# Revit family: LVS1HD
name_source: partatom
category: Communication Devices
units: mm (PartAtom-declared; Revit-internal decimal feet)

## family parameters
Cut with Voids When Loaded = No
Host = Face
Maintain Annotation Orientation = No
OmniClass Number = 23.85.80.11.27
OmniClass Title = Lighting Controls
Part Type = Normal
Room Calculation Point = No
Round Connector Dimension = Use Diameter
Shared = Yes

## types (1)
- LVS1HD
    Assembly Code = D5090
    Blue = Plastic - Blue
    Default Elevation = 48 "
    Description = Our LVS1HD heavy duty wall switch is ideal for high abuse applications where standard plastic low voltage wall switch stations are not suitable. The LVS1HD looks like a standard wall switch except has a spring loaded return to center toggle action that can be connected to lighting controls expecting a dry contact momentary input.
    Feartures = • Gang-able, uses standard switch plate (not supplied)
• Abuse resistant nylon toggle
• UL 94V-2 flammability rating
• Heavy duty Silver Alloy contacts
• Compatible with CX panel low voltage inputs
• Use NXCI Contact Interface module for compatibility with NX™
distributed controls
• UL listed, CSA certified
• Low voltage device: 24 VDC
    Housing Material = Metal-Galvanized_Steel
    Manufacturer = NX Lighting Controls
    Metal = Steel, Non-Alloy
    Model = LVS1HD
    Switch = Porcelain, Ivory
    Type Comments = Heavy Duty Low Voltage Wall Switch
    URL = https://www.currentlighting.com
    Warranty = 5-Years Warranty

## geometry (parser evidence)
native form markers: Sweep x2
no freeform markers — native parametric forms only
